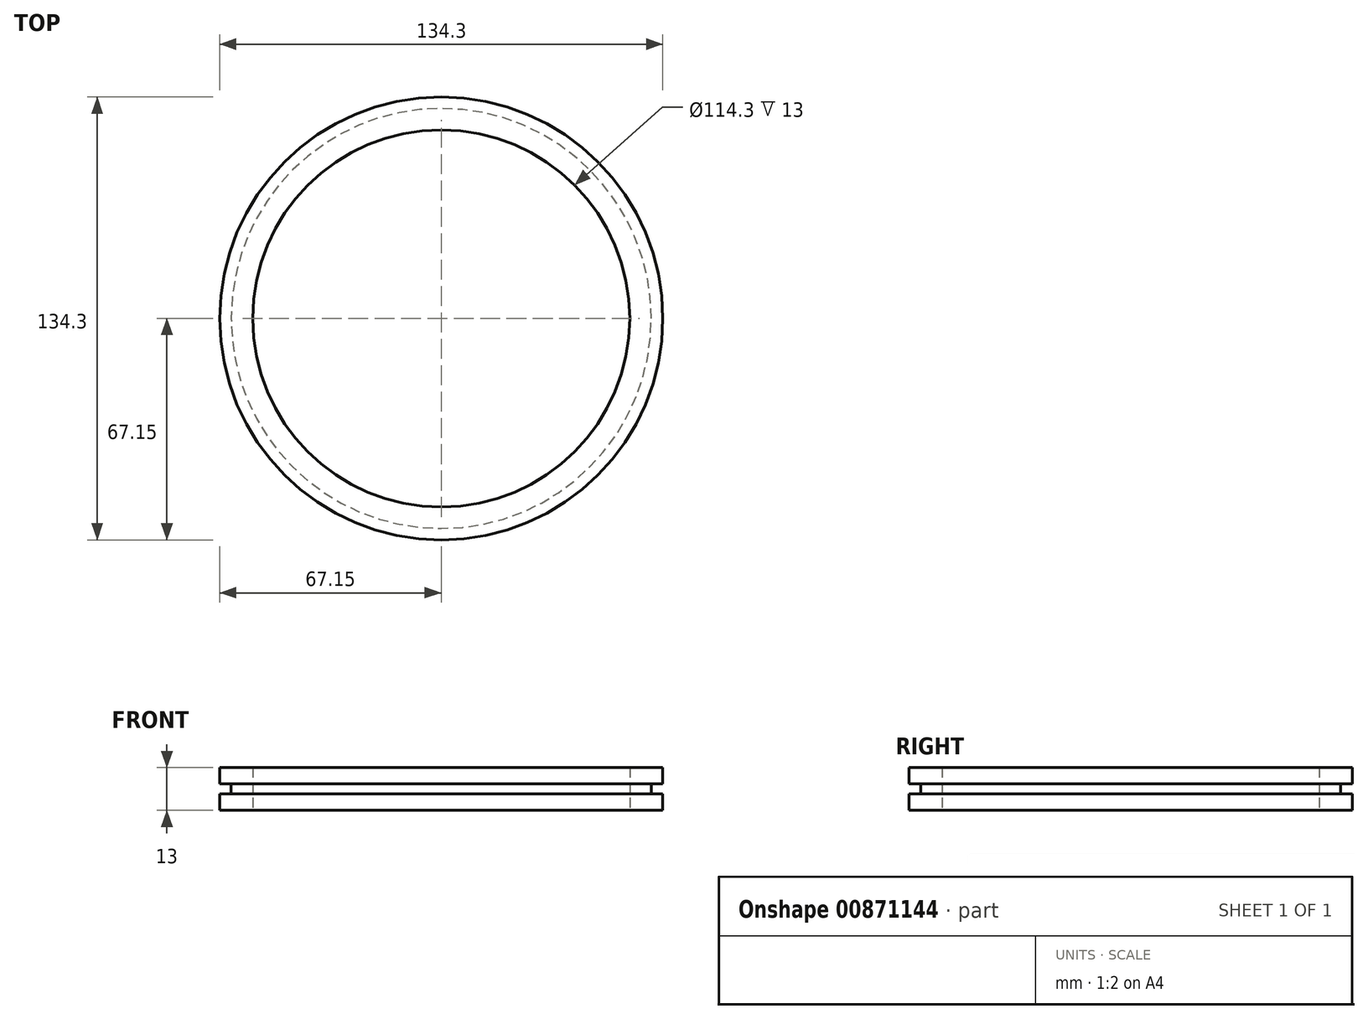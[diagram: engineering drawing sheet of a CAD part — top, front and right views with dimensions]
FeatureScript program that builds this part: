
annotation { "Feature Type Name" : "Feature", "Feature Type Description" : "" }
export const myFeature = defineFeature(function(context is Context, id is Id, definition is map)
    precondition{}
    {
        {
            var Q0;
            Q0=qCreatedBy(makeId("Top.planeOp"),FACE);
            var sketch = newSketch(context, id + "F0", { "sketchPlane" : qUnion([Q0])});
            skCircle(sketch, "E0", {"center": v(0, 0) * mm, "radius": 57.15 * mm});
            skCircle(sketch, "E1", {"center": v(0, 0) * mm, "radius": 63.66 * mm});
            skSolve(sketch);
        }
        {
            var Q0;
            Q0=makeQuery(id+"F0.imprint","IMPRINT",FACE,{"disambiguationData":[TD([[makeQuery(id+"F0.imprint","IMPRINT",EDGE,{"derivedFrom":sQuery(id+"F0.wireOp",EDGE,"E0")}),-1.0]])]});
            extrude(context, id + "F1", {"entities" : qUnion([Q0]), "depth" : 3 * mm, "offsetDistance" : 25.4 * mm});
        }
        {
            var Q0;
            Q0=makeQuery(id+"F0.imprint","IMPRINT",FACE,{"disambiguationData":[TD([[makeQuery(id+"F0.imprint","IMPRINT",EDGE,{"derivedFrom":sQuery(id+"F0.wireOp",EDGE,"E0")}),-1.0]])]});
            var sketch = newSketch(context, id + "F2", { "sketchPlane" : qUnion([Q0])});
            skCircle(sketch, "E2", {"center": v(0, 0) * mm, "radius": 57.15 * mm});
            skCircle(sketch, "E3", {"center": v(0, 0) * mm, "radius": 67.15 * mm});
            skSolve(sketch);
        }
        {
            var Q0;
            Q0=makeQuery(id+"F2.imprint","IMPRINT",FACE,{"disambiguationData":[TD([[makeQuery(id+"F2.imprint","IMPRINT",EDGE,{"derivedFrom":sQuery(id+"F2.wireOp",EDGE,"E3")}),1.0]])]});
            var Q1;
            Q1=makeQuery(id+"F0.imprint","IMPRINT",FACE,{"disambiguationData":[TD([[makeQuery(id+"F0.imprint","IMPRINT",EDGE,{"derivedFrom":sQuery(id+"F0.wireOp",EDGE,"E0")}),-1.0]])]});
            extrude(context, id + "F3", {"entities" : qUnion([Q0, Q1]), "operationType" : NewBodyOperationType.ADD, "oppositeDirection" : true, "depth" : 5 * mm, "offsetDistance" : 25.4 * mm});
        }
        {
            var Q0;
            Q0=makeQuery(id+"F1.opExtrude","CAP_FACE",FACE,{"disambiguationData":[OSD([sQuery(id+"F0.wireOp",EDGE,"E0"),sQuery(id+"F0.wireOp",EDGE,"E1")])],"isStart":false});
            var sketch = newSketch(context, id + "F4", { "sketchPlane" : qUnion([Q0])});
            skCircle(sketch, "E4", {"center": v(0, 0) * mm, "radius": 57.15 * mm});
            skCircle(sketch, "E5", {"center": v(0, 0) * mm, "radius": 67.15 * mm});
            skSolve(sketch);
        }
        {
            var Q0;
            Q0=makeQuery(id+"F4.imprint","IMPRINT",FACE,{"disambiguationData":[TD([[makeQuery(id+"F4.imprint","IMPRINT",EDGE,{"derivedFrom":sQuery(id+"F4.wireOp",EDGE,"E5")}),1.0]])]});
            var Q1;
            Q1=makeQuery(id+"F4.imprint","IMPRINT",FACE,{"disambiguationData":[TD([[makeQuery(id+"F4.imprint","IMPRINT",EDGE,{"derivedFrom":sQuery(id+"F4.wireOp",EDGE,"E4")}),-1.0]])]});
            extrude(context, id + "F5", {"entities" : qUnion([Q0, Q1]), "operationType" : NewBodyOperationType.ADD, "depth" : 5 * mm, "offsetDistance" : 25.4 * mm});
        }
    });
